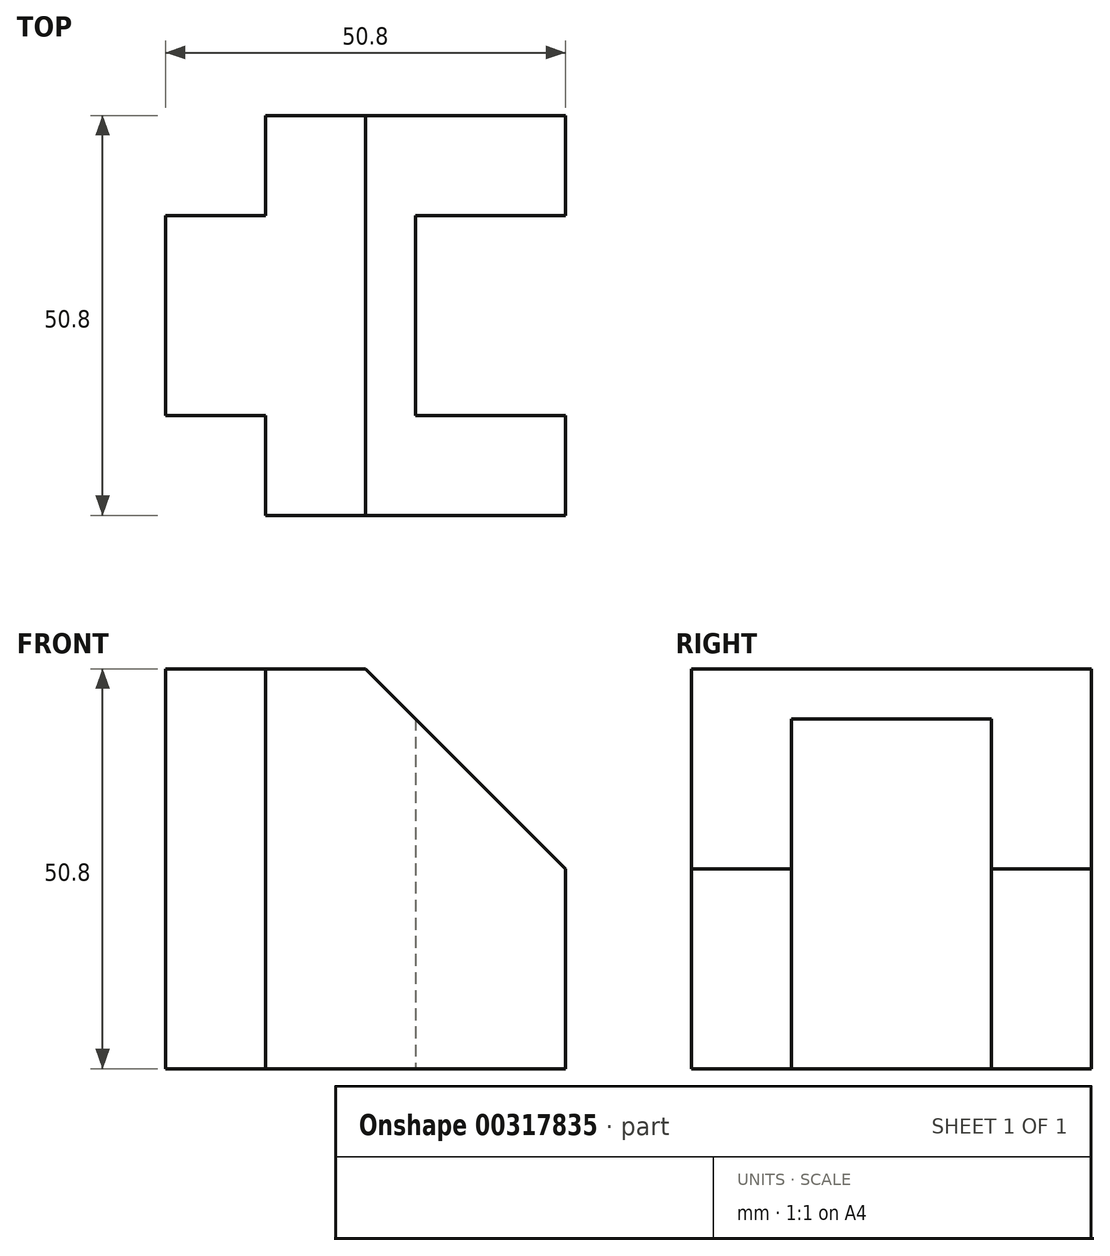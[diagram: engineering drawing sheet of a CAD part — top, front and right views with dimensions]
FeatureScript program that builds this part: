
annotation { "Feature Type Name" : "Feature", "Feature Type Description" : "" }
export const myFeature = defineFeature(function(context is Context, id is Id, definition is map)
    precondition{}
    {
        {
            var Q0;
            Q0=qCreatedBy(makeId("Front.planeOp"),FACE);
            var sketch = newSketch(context, id + "F0", { "sketchPlane" : qUnion([Q0])});
            skLineSegment(sketch, "E0", {"start": v(0, 0) * mm, "end": v(0, 50.8) * mm});
            skLineSegment(sketch, "E1", {"start": v(0, 50.8) * mm, "end": v(25.4, 50.8) * mm});
            skLineSegment(sketch, "E2", {"start": v(25.4, 50.8) * mm, "end": v(50.8, 25.4) * mm});
            skLineSegment(sketch, "E3", {"start": v(50.8, 25.4) * mm, "end": v(50.8, 0) * mm});
            skLineSegment(sketch, "E4", {"start": v(50.8, 0) * mm, "end": v(0, 0) * mm});
            skSolve(sketch);
        }
        {
            var Q0;
            Q0 = qSketchRegion(id + "F0", true);
            extrude(context, id + "F1", {"entities" : qUnion([Q0]), "depth" : 50.8 * mm});
        }
        {
            var Q0;
            Q0=qCreatedBy(makeId("Top.planeOp"),FACE);
            var sketch = newSketch(context, id + "F2", { "sketchPlane" : qUnion([Q0])});
            skLineSegment(sketch, "E5.bottom", {"start": v(0, 0) * mm, "end": v(12.7, 0) * mm});
            skLineSegment(sketch, "E5.top", {"start": v(0, -12.7) * mm, "end": v(12.7, -12.7) * mm});
            skLineSegment(sketch, "E5.left", {"start": v(0, 0) * mm, "end": v(0, -12.7) * mm});
            skLineSegment(sketch, "E5.right", {"start": v(12.7, 0) * mm, "end": v(12.7, -12.7) * mm});
            skLineSegment(sketch, "E6.bottom", {"start": v(0, -50.8) * mm, "end": v(12.7, -50.8) * mm});
            skLineSegment(sketch, "E6.top", {"start": v(0, -38.1) * mm, "end": v(12.7, -38.1) * mm});
            skLineSegment(sketch, "E6.left", {"start": v(0, -50.8) * mm, "end": v(0, -38.1) * mm});
            skLineSegment(sketch, "E6.right", {"start": v(12.7, -50.8) * mm, "end": v(12.7, -38.1) * mm});
            skLineSegment(sketch, "E7.bottom", {"start": v(50.8, -12.7) * mm, "end": v(31.75, -12.7) * mm});
            skLineSegment(sketch, "E7.top", {"start": v(50.8, -38.1) * mm, "end": v(31.75, -38.1) * mm});
            skLineSegment(sketch, "E7.left", {"start": v(50.8, -12.7) * mm, "end": v(50.8, -38.1) * mm});
            skLineSegment(sketch, "E7.right", {"start": v(31.75, -12.7) * mm, "end": v(31.75, -38.1) * mm});
            skSolve(sketch);
        }
        {
            var Q0;
            Q0 = qSketchRegion(id + "F2", true);
            extrude(context, id + "F3", {"entities" : qUnion([Q0]), "operationType" : NewBodyOperationType.REMOVE, "endBound" : BoundingType.THROUGH_ALL, "depth" : 25.4 * mm});
        }
    });
